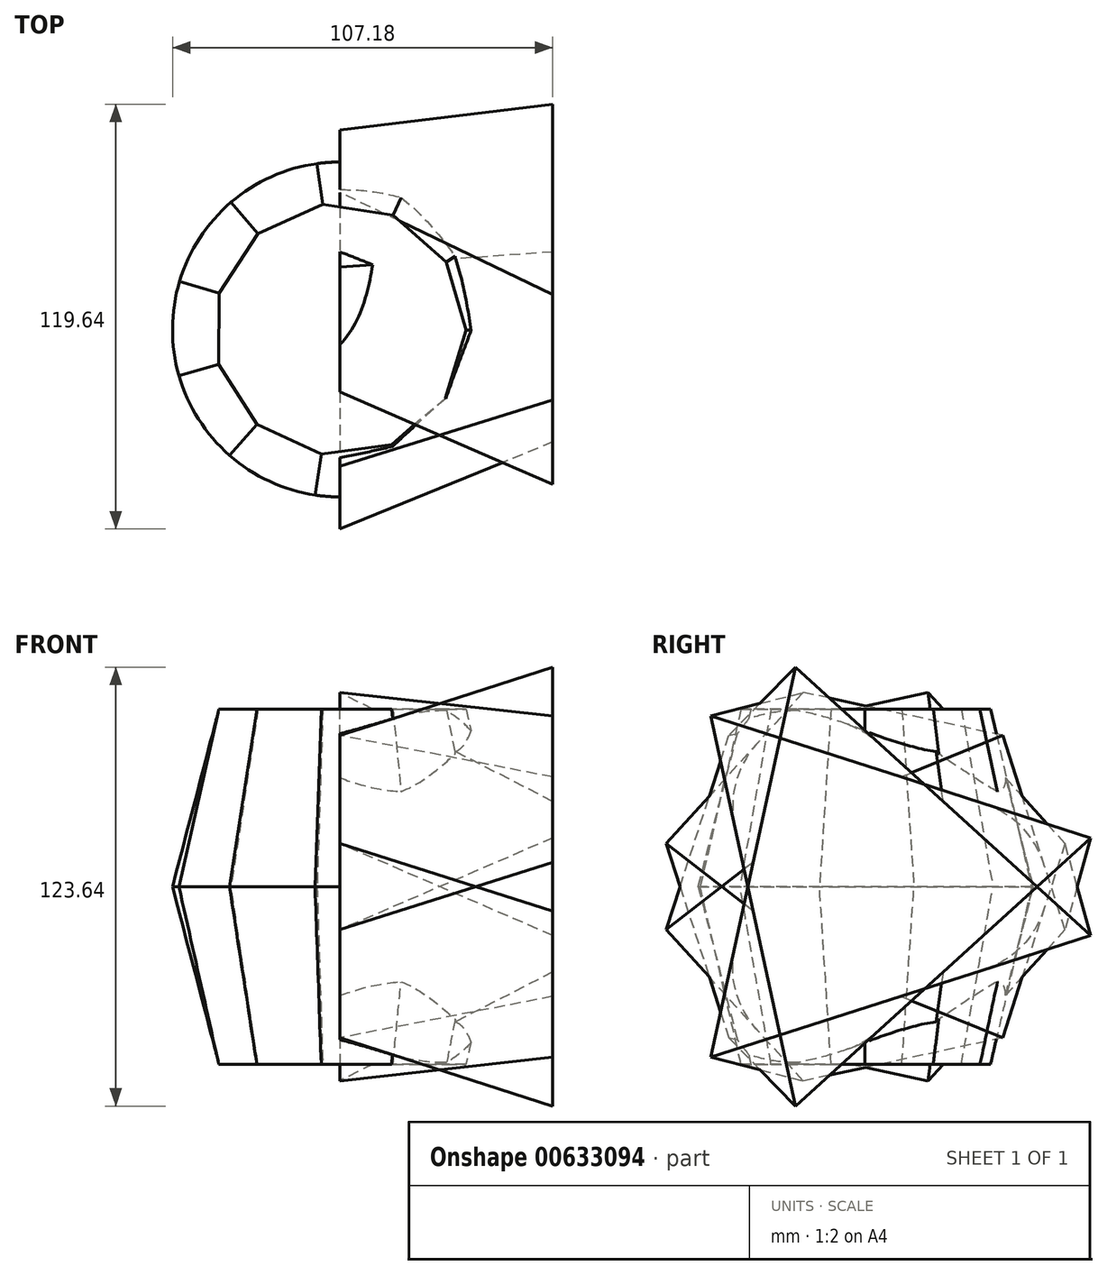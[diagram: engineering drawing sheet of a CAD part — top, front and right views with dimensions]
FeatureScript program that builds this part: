
annotation { "Feature Type Name" : "Feature", "Feature Type Description" : "" }
export const myFeature = defineFeature(function(context is Context, id is Id, definition is map)
    precondition{}
    {
        {
            var Q0;
            Q0=qCreatedBy(makeId("Top.planeOp"),FACE);
            var sketch = newSketch(context, id + "F0", { "sketchPlane" : qUnion([Q0])});
            skCircle(sketch, "E0", {"center": v(0, 0) * mm, "radius": 47.18 * mm});
            skSolve(sketch);
        }
        {
            var Q0;
            Q0=qCreatedBy(makeId("Top.planeOp"),FACE);
            cPlane(context, id + "F1", {"entities" : qUnion([Q0]), "cplaneType" : CPlaneType.OFFSET, "offset" : 50 * mm, "width" : 152.4 * mm, "height" : 152.4 * mm});
        }
        {
            var Q0;
            Q0=qCreatedBy(id+"F1.planeOp",FACE);
            var sketch = newSketch(context, id + "F2", { "sketchPlane" : qUnion([Q0])});
            skCircle(sketch, "E1.cCircle", {"center": v(0, 0) * mm, "radius": 34.08 * mm, "construction": true});
            skLineSegment(sketch, "E1.0", {"start": v(-5.27, -35.12) * mm, "end": v(-23.42, -26.7) * mm});
            skLineSegment(sketch, "E1.1", {"start": v(-23.42, -26.7) * mm, "end": v(-34.14, -9.8) * mm});
            skLineSegment(sketch, "E1.2", {"start": v(-34.14, -9.8) * mm, "end": v(-34.02, 10.21) * mm});
            skLineSegment(sketch, "E1.3", {"start": v(-34.02, 10.21) * mm, "end": v(-23.1, 26.98) * mm});
            skLineSegment(sketch, "E1.4", {"start": v(-23.1, 26.98) * mm, "end": v(-4.84, 35.19) * mm});
            skLineSegment(sketch, "E1.5", {"start": v(-4.84, 35.19) * mm, "end": v(14.95, 32.22) * mm});
            skLineSegment(sketch, "E1.6", {"start": v(14.95, 32.22) * mm, "end": v(30, 19.02) * mm});
            skLineSegment(sketch, "E1.7", {"start": v(30, 19.02) * mm, "end": v(35.52, -0.22) * mm});
            skLineSegment(sketch, "E1.8", {"start": v(35.52, -0.22) * mm, "end": v(29.76, -19.38) * mm});
            skLineSegment(sketch, "E1.9", {"start": v(29.76, -19.38) * mm, "end": v(14.56, -32.4) * mm});
            skLineSegment(sketch, "E1.10", {"start": v(14.56, -32.4) * mm, "end": v(-5.27, -35.12) * mm});
            skPoint(sketch, "E1.0.midPoint", {"position": v(-14.35, -30.91) * mm});
            skSolve(sketch);
        }
        {
            var Q0;
            Q0=makeQuery(id+"F2.imprint","IMPRINT",FACE,{"disambiguationData":[TD([[makeQuery(id+"F2.imprint","IMPRINT",EDGE,{"derivedFrom":sQuery(id+"F2.wireOp",EDGE,"E1.0")}),-1.0]])]});
            var Q1;
            Q1=makeQuery(id+"F0.imprint","IMPRINT",FACE,{"disambiguationData":[TD([[makeQuery(id+"F0.imprint","IMPRINT",EDGE,{"derivedFrom":sQuery(id+"F0.wireOp",EDGE,"E0")}),1.0]])]});
            loft(context, id + "F3", {"sheetProfilesArray" : [{ "sheetProfileEntities" : qUnion([Q0]) }, { "sheetProfileEntities" : qUnion([Q1]) }]});
        }
        {
            var Q0;
            Q0=qCreatedBy(makeId("Right.planeOp"),FACE);
            cPlane(context, id + "F4", {"entities" : qUnion([Q0]), "cplaneType" : CPlaneType.OFFSET, "offset" : 60 * mm, "width" : 152.4 * mm, "height" : 152.4 * mm});
        }
        {
            var Q0;
            Q0=qCreatedBy(id+"F4.planeOp",FACE);
            var sketch = newSketch(context, id + "F5", { "sketchPlane" : qUnion([Q0])});
            skCircle(sketch, "E2.cCircle", {"center": v(0, 0) * mm, "radius": 32.46 * mm, "construction": true});
            skLineSegment(sketch, "E2.0", {"start": v(63.45, -13.75) * mm, "end": v(-43.63, -48.07) * mm});
            skLineSegment(sketch, "E2.1", {"start": v(-43.63, -48.07) * mm, "end": v(-19.82, 61.82) * mm});
            skLineSegment(sketch, "E2.2", {"start": v(-19.82, 61.82) * mm, "end": v(63.45, -13.75) * mm});
            skPoint(sketch, "E2.0.midPoint", {"position": v(9.9, -30.91) * mm});
            skSolve(sketch);
        }
        {
            var Q0;
            Q0=qCreatedBy(makeId("Right.planeOp"),FACE);
            var sketch = newSketch(context, id + "F6", { "sketchPlane" : qUnion([Q0])});
            skCircle(sketch, "E3.cCircle", {"center": v(0, 0) * mm, "radius": 49.78 * mm, "construction": true});
            skLineSegment(sketch, "E3.0", {"start": v(38.6, -42.6) * mm, "end": v(-17.6, -54.72) * mm});
            skLineSegment(sketch, "E3.1", {"start": v(-17.6, -54.72) * mm, "end": v(-56.19, -12.13) * mm});
            skLineSegment(sketch, "E3.2", {"start": v(-56.19, -12.13) * mm, "end": v(-38.6, 42.6) * mm});
            skLineSegment(sketch, "E3.3", {"start": v(-38.6, 42.6) * mm, "end": v(17.6, 54.72) * mm});
            skLineSegment(sketch, "E3.4", {"start": v(17.6, 54.72) * mm, "end": v(56.19, 12.13) * mm});
            skLineSegment(sketch, "E3.5", {"start": v(56.19, 12.13) * mm, "end": v(38.6, -42.6) * mm});
            skPoint(sketch, "E3.0.midPoint", {"position": v(10.5, -48.66) * mm});
            skSolve(sketch);
        }
        {
            var Q1;
            Q1=makeQuery(id+"F5.imprint","IMPRINT",FACE,{"disambiguationData":[TD([[makeQuery(id+"F5.imprint","IMPRINT",EDGE,{"derivedFrom":sQuery(id+"F5.wireOp",EDGE,"E2.0")}),-1.0]])]});
            var Q2;
            Q2=makeQuery(id+"F6.imprint","IMPRINT",FACE,{"disambiguationData":[TD([[makeQuery(id+"F6.imprint","IMPRINT",EDGE,{"derivedFrom":sQuery(id+"F6.wireOp",EDGE,"E3.0")}),-1.0]])]});
            loft(context, id + "F7", {"operationType" : NewBodyOperationType.ADD, "sheetProfilesArray" : [{ "sheetProfileEntities" : qUnion([Q1]) }, { "sheetProfileEntities" : qUnion([Q2]) }]});
        }
        {
            var Q0;
            Q0=makeQuery(id+"F3.opLoft","SWEPT_BODY",BODY,{"disambiguationData":[OSD([makeQuery(id+"F0.imprint","IMPRINT",FACE,{"disambiguationData":[TD([[makeQuery(id+"F0.imprint","IMPRINT",EDGE,{"derivedFrom":sQuery(id+"F0.wireOp",EDGE,"E0")}),1.0]])]}),makeQuery(id+"F2.imprint","IMPRINT",FACE,{"disambiguationData":[TD([[makeQuery(id+"F2.imprint","IMPRINT",EDGE,{"derivedFrom":sQuery(id+"F2.wireOp",EDGE,"E1.0")}),-1.0]])]})])]});
            var Q1;
            Q1=qCreatedBy(makeId("Top.planeOp"),FACE);
            mirror(context, id + "F8", {"entities" : qUnion([Q0]), "mirrorPlane" : qUnion([Q1])});
        }
    });
